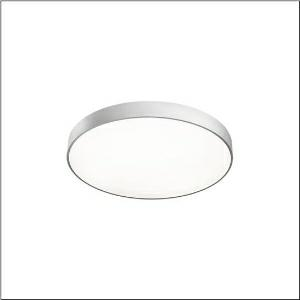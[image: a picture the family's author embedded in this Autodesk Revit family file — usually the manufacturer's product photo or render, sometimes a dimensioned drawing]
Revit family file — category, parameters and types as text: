
# Revit family: round_21_m_51mr36fd0421s
name_source: partatom
category: Lighting Fixtures
units: mm (PartAtom-declared; Revit-internal decimal feet)

## family parameters
Cut with Voids When Loaded = No
Host = Face
Light Source = No
Part Type = Normal
Room Calculation Point = No
Round Connector Dimension = Use Diameter
Shared = No

## types (1)
- Round 21 M (1 x LED, 7810 lm, 54.9 W, 4000K)
    Apparent Load = 55 VA
    CIE Flux Codes = 49 80 96 100 100
    Color Rendering = 80
    Color Temperature = 4000K
    Default Elevation = 1800 mm
    Description = Round 21 M, wall and ceiling luminaire, primary optical cover: cover, of PMMA, opal, light emission: direct distribution, primary light characteristic: symmetric, installation type: surface-mounted, suspended mounting, LED, rated luminous flux: 7.810lm, luminous efficacy: 142lm/W, light colour: 840, colour temperature: 4000K, control gear: DALI 2, with terminal, 5-pole, mains connection: 230V, AC, 50/60Hz, rated input power: 55W, housing, of aluminium, coated, silver, diameter: 600mm, height: 62mm, protection rating (complete): IP40, insulation class (complete): insulation class I (protective earthing), certification: CE, impact resistance: IK04, permissible operating ambient temperature: -10..+35°C, packaging unit: 1 piece
    Height = 87 mm
    Lamp = 1 x LED
    Lamp Light Flux = 7810 lm
    Lamp Power = 54.9 W
    Lamp count = 1
    Length = 600 mm
    Luminous efficacy = 142 lm/W
    Manufacturer = Siteco
    ModVariant = No
    Model = 51MR36FD0421S
    Mounting Place = Ceiling
    Mounting Type = Surface mounted
    Number of Poles = 1
    OnlyDefault = Yes
    Power Factor = 1
    Product Name = Round 21 M
    Product group = wall and ceiling luminaire
    ProductGroupID = 304
    Protection Class = Protection class I
    Protection Degree = IP 40
    RLX_Detail_Level = 1
    RLX_Emergency_Light_Flux = 0 lm
    RLX_Emergency_Type = 0
    RLX_Emergency_Type_DB = No
    RlxData = <blob elided: 14829 chars, md5=9c5a2fd3>
    Socket = socket
    Standby Power = 0 W
    System Light Flux = 7810 lm
    System Power = 55 W
    Type Comments = Product without accessories
    Type Image = l_1258303.jpg
    URL = http://relux.com
    VarID = ---
    Voltage = 0 V
    Weight = 0.00 kg
    Width = 0 mm  [stored 0 ft]

note: [stored X ft] marks values corroborated as IEEE doubles in the binary element streams (Revit-internal decimal feet)

## geometry (parser evidence)
native form markers: Sweep x9
no freeform markers — native parametric forms only
